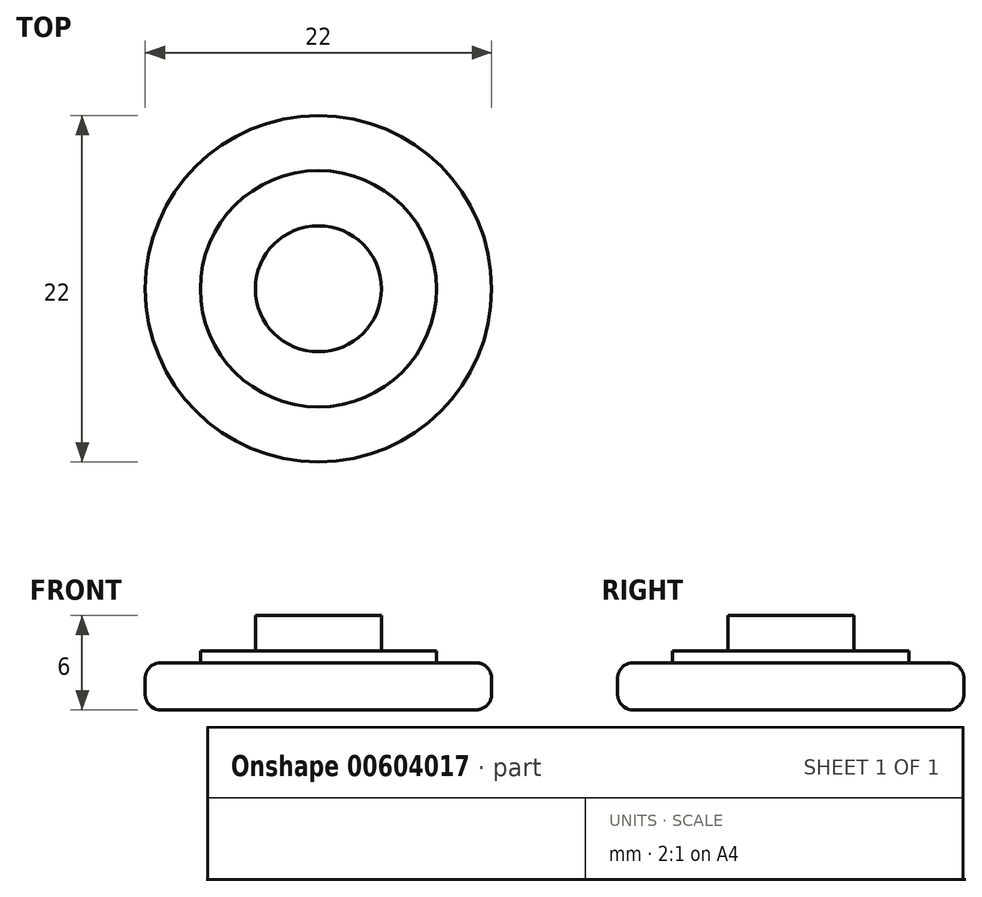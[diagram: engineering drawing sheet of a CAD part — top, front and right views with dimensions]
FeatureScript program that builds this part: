
annotation { "Feature Type Name" : "Feature", "Feature Type Description" : "" }
export const myFeature = defineFeature(function(context is Context, id is Id, definition is map)
    precondition{}
    {
        {
            var Q0;
            Q0=qCreatedBy(makeId("Top.planeOp"),FACE);
            var sketch = newSketch(context, id + "F0", { "sketchPlane" : qUnion([Q0])});
            skCircle(sketch, "E0", {"center": v(0, 0) * mm, "radius": 11 * mm});
            skCircle(sketch, "E1", {"center": v(0, 0) * mm, "radius": 7.5 * mm});
            skCircle(sketch, "E2", {"center": v(0, 0) * mm, "radius": 4 * mm});
            skSolve(sketch);
        }
        {
            var Q0;
            Q0=makeQuery(id+"F0.imprint","IMPRINT",FACE,{"disambiguationData":[TD([[makeQuery(id+"F0.imprint","IMPRINT",EDGE,{"derivedFrom":sQuery(id+"F0.wireOp",EDGE,"E0")}),1.0]])]});
            extrude(context, id + "F1", {"entities" : qUnion([Q0]), "depth" : 3 * mm, "offsetDistance" : 25 * mm});
        }
        {
            var Q0;
            Q0=makeQuery(id+"F0.imprint","IMPRINT",FACE,{"disambiguationData":[TD([[makeQuery(id+"F0.imprint","IMPRINT",EDGE,{"derivedFrom":sQuery(id+"F0.wireOp",EDGE,"E1")}),1.0]])]});
            extrude(context, id + "F2", {"entities" : qUnion([Q0]), "operationType" : NewBodyOperationType.ADD, "depth" : 3.75 * mm, "offsetDistance" : 25 * mm});
        }
        {
            var Q0;
            Q0=makeQuery(id+"F0.imprint","IMPRINT",FACE,{"disambiguationData":[TD([[makeQuery(id+"F0.imprint","IMPRINT",EDGE,{"derivedFrom":sQuery(id+"F0.wireOp",EDGE,"E2")}),1.0]])]});
            extrude(context, id + "F3", {"entities" : qUnion([Q0]), "operationType" : NewBodyOperationType.ADD, "depth" : 6 * mm, "offsetDistance" : 25 * mm});
        }
        {
            var Q0;
            Q0=makeQuery(id+"F1.opExtrude","CAP_EDGE",EDGE,{"disambiguationData":[OSD([sQuery(id+"F0.wireOp",EDGE,"E0")])],"isStart":true});
            var Q1;
            Q1=makeQuery(id+"F1.opExtrude","CAP_EDGE",EDGE,{"disambiguationData":[OSD([sQuery(id+"F0.wireOp",EDGE,"E0")])],"isStart":false});
            fillet(context, id + "F4", {"entities" : qUnion([Q0, Q1]), "radius" : 1 * mm, "tangentPropagation" : true, "allowEdgeOverflow" : false});
        }
    });
